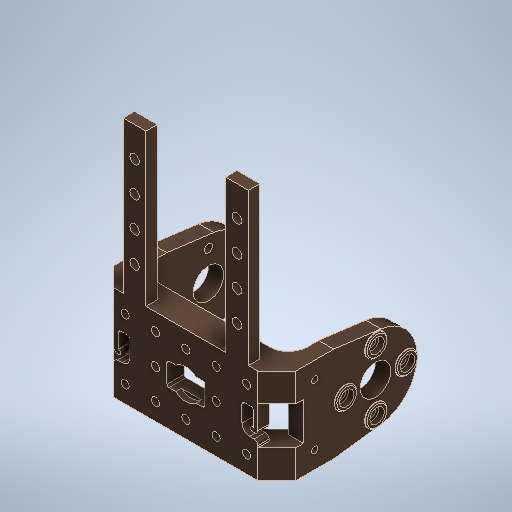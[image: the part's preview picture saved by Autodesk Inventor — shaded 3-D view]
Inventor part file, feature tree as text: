
AUTODESK INVENTOR PART (.ipt)
format: ipt  version: 2025 (Build 290162000, 162)  size: 1,441,280 bytes
history: native  units: in
note: dims shown in document units (in); Inventor stores cm internally (conversion verified against a paired STEP export)
features: extrude x2, sketch x2, other x2, direct_edit x1, imported_body x1
ambient origin geometry x8: Origin, YZ Plane, XZ Plane, XY Plane, X Axis, Y Axis, Z Axis, Center Point
bodies: Solid1 (feature_tree)
feature tree (8):
  direct_edit  "Direct Edit1"
  extrude  "Extrusión3"  Depth=0.0394in
  extrude  "Extrusión10"  Depth=0.1181in
  sketch  "Boceto5"  dims[d1=0.0394in d2=0.0394in]
  sketch  "Boceto15"  dims[d16=1.5748in d17=0.0in d70=0.1181in d71=0.2362in d72=0.2362in d73=0.8268in d74=0.0984in d75=0.0984in d76=0.3192in d77=0.1181in d78=0.0984in d79=0.315in d80=0.1575in d81=0.315in d84=0.0in d85=0.0in d86=0.1181in d87=1.063in d48=0.0197in d49=0.0344in d50=0.0197in d51=0.0344in]
  imported_body  "Base1"
  other  "Size1"
  other  "Size2"
